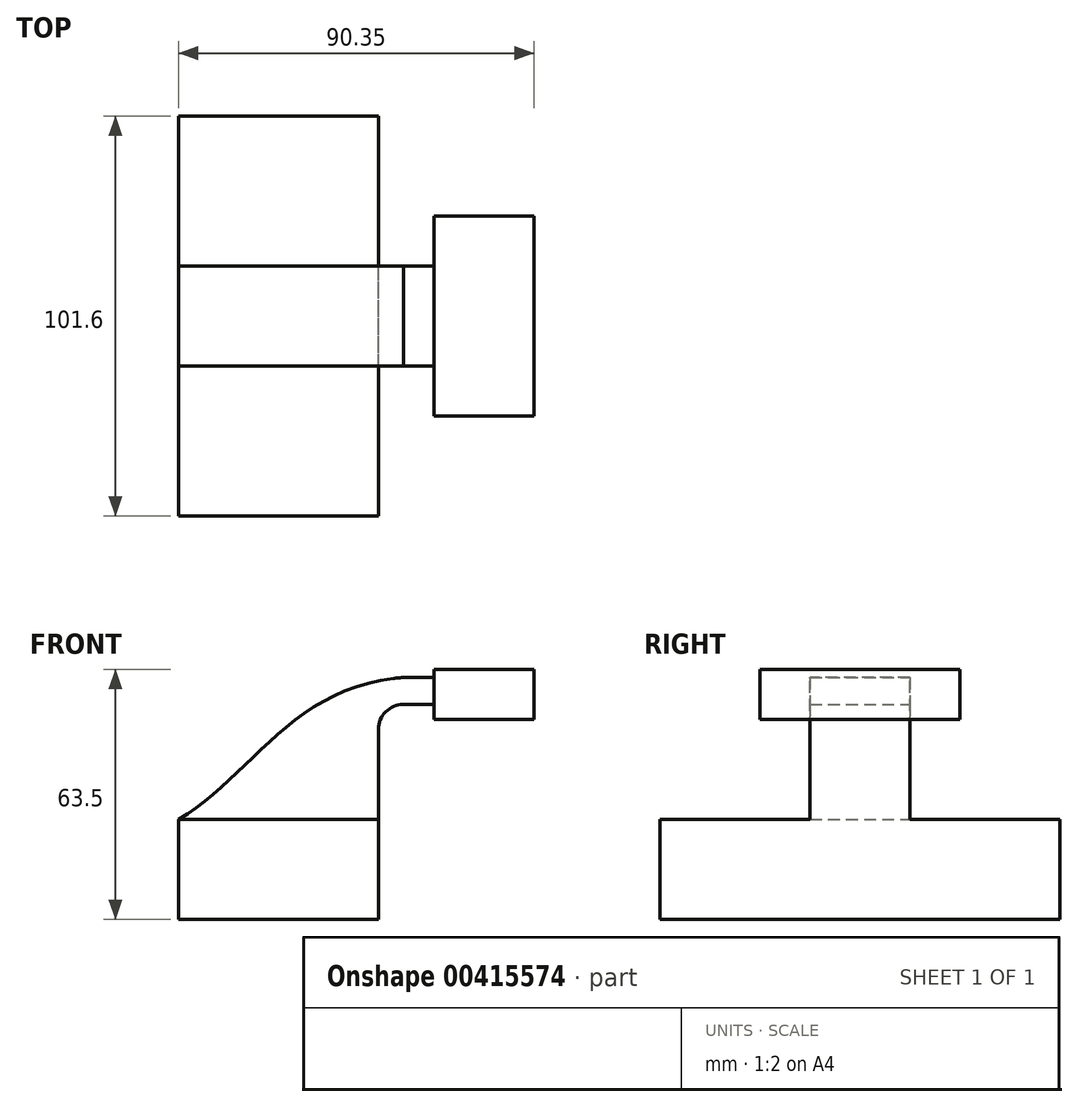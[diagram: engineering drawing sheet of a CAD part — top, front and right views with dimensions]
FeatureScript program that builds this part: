
annotation { "Feature Type Name" : "Feature", "Feature Type Description" : "" }
export const myFeature = defineFeature(function(context is Context, id is Id, definition is map)
    precondition{}
    {
        {
            var Q0;
            Q0=qCreatedBy(makeId("Front.planeOp"),FACE);
            var sketch = newSketch(context, id + "F0", { "sketchPlane" : qUnion([Q0])});
            skLineSegment(sketch, "E0.bottom", {"start": v(39.55, 50.5) * mm, "end": v(64.95, 50.5) * mm});
            skLineSegment(sketch, "E0.top", {"start": v(39.55, 37.8) * mm, "end": v(64.95, 37.8) * mm});
            skLineSegment(sketch, "E0.left", {"start": v(39.55, 50.5) * mm, "end": v(39.55, 37.8) * mm});
            skLineSegment(sketch, "E0.right", {"start": v(64.95, 50.5) * mm, "end": v(64.95, 37.8) * mm});
            skLineSegment(sketch, "E1", {"start": v(25.4, 12.4) * mm, "end": v(25.4, 35.26) * mm});
            skArc(sketch, "E2", {"start": v(25.4, 35.26) * mm, "mid": v(27.26, 39.75) * mm, "end": v(31.75, 41.6) * mm});
            skLineSegment(sketch, "E3", {"start": v(31.75, 41.6) * mm, "end": v(55.07, 41.6) * mm});
            skLineSegment(sketch, "E4.bottom", {"start": v(25.4, 12.4) * mm, "end": v(-25.4, 12.4) * mm});
            skLineSegment(sketch, "E4.top", {"start": v(25.4, -13) * mm, "end": v(-25.4, -13) * mm});
            skLineSegment(sketch, "E4.left", {"start": v(25.4, 12.4) * mm, "end": v(25.4, -13) * mm});
            skLineSegment(sketch, "E4.right", {"start": v(-25.4, 12.4) * mm, "end": v(-25.4, -13) * mm});
            skPoint(sketch, "E4.middle", {"position": v(0, -0.3) * mm});
            skLineSegment(sketch, "E5.0", {"start": v(31.75, 48.46) * mm, "end": v(55.07, 48.46) * mm});
            skArc(sketch, "E5.1", {"start": v(18.54, 35.26) * mm, "mid": v(22.41, 44.6) * mm, "end": v(31.75, 48.46) * mm});
            skLineSegment(sketch, "E5.2", {"start": v(18.54, 12.68) * mm, "end": v(18.54, 35.26) * mm});
            skFitSpline(sketch, "E6", {"points": [v(-25.4, 12.4) * mm, v(31.75, 48.46) * mm], "startDerivative": vector(55.62, 32.05) * mm, "endDerivative": vector(84.92, 5.88) * mm});
            skLineSegment(sketch, "E7", {"start": v(55.07, 50.5) * mm, "end": v(55.07, 37.8) * mm});
            skSolve(sketch);
        }
        {
            var Q0;
            Q0=makeQuery(id+"F0.imprint","IMPRINT",FACE,{"disambiguationData":[TD([[makeQuery(id+"F0.imprint","IMPRINT",EDGE,{"derivedFrom":sQuery(id+"F0.wireOp",EDGE,"E4.bottom")}),1.0]])]});
            extrude(context, id + "F1", {"entities" : qUnion([Q0]), "endBound" : BoundingType.SYMMETRIC, "depth" : 101.6 * mm});
        }
        {
            var Q0;
            {var subQ0=sQuery(id+"F0.wireOp",EDGE,"E0.right");Q0=makeQuery(id+"F0.imprint","IMPRINT",FACE,{"disambiguationData":[TD([[makeQuery(id+"F0.imprint","IMPRINT",EDGE,{"derivedFrom":subQ0}),-1.0]])]});}
            var Q1;
            {var subQ0=sQuery(id+"F0.wireOp",EDGE,"E0.left");var subQ1=sQuery(id+"F0.wireOp",EDGE,"E0.top");var subQ2=makeQuery(id+"F0.imprint","INTERSECT",VERTEX,{"derivedFrom":[subQ1,subQ0]});Q1=makeQuery(id+"F0.imprint","IMPRINT",FACE,{"disambiguationData":[TD([[makeQuery(id+"F0.imprint","IMPRINT",EDGE,{"disambiguationData":[TD([[subQ2,-1.0]])],"derivedFrom":subQ1}),1.0]])]});}
            var Q2;
            {var subQ0=sQuery(id+"F0.wireOp",EDGE,"E0.left");var subQ1=sQuery(id+"F0.wireOp",EDGE,"E0.bottom");var subQ2=makeQuery(id+"F0.imprint","INTERSECT",VERTEX,{"derivedFrom":[subQ1,subQ0]});Q2=makeQuery(id+"F0.imprint","IMPRINT",FACE,{"disambiguationData":[TD([[makeQuery(id+"F0.imprint","IMPRINT",EDGE,{"disambiguationData":[TD([[subQ2,-1.0]])],"derivedFrom":subQ1}),-1.0]])]});}
            var Q3;
            {var subQ0=sQuery(id+"F0.wireOp",EDGE,"E5.0");var subQ1=sQuery(id+"F0.wireOp",EDGE,"E0.left");var subQ2=makeQuery(id+"F0.imprint","INTERSECT",VERTEX,{"derivedFrom":[subQ1,subQ0]});Q3=makeQuery(id+"F0.imprint","IMPRINT",FACE,{"disambiguationData":[TD([[makeQuery(id+"F0.imprint","IMPRINT",EDGE,{"disambiguationData":[TD([[subQ2,-1.0]])],"derivedFrom":subQ1}),1.0]])]});}
            extrude(context, id + "F2", {"entities" : qUnion([Q0, Q1, Q2, Q3]), "operationType" : NewBodyOperationType.ADD, "endBound" : BoundingType.SYMMETRIC, "depth" : 50.8 * mm});
        }
        {
            var Q0;
            Q0=makeQuery(id+"F0.imprint","IMPRINT",FACE,{"disambiguationData":[TD([[makeQuery(id+"F0.imprint","IMPRINT",EDGE,{"derivedFrom":sQuery(id+"F0.wireOp",EDGE,"E1")}),1.0]])]});
            extrude(context, id + "F3", {"entities" : qUnion([Q0]), "operationType" : NewBodyOperationType.ADD, "endBound" : BoundingType.SYMMETRIC, "depth" : 25.4 * mm});
        }
    });
